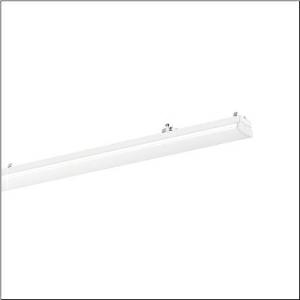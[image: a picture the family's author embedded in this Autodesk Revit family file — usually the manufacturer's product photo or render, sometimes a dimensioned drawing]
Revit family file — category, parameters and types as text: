
# Revit family: licross_r__11_recessed_opal_ho_51te1ddn46xm_35a1
name_source: partatom
category: Lighting Fixtures
units: mm (PartAtom-declared; Revit-internal decimal feet)

## family parameters
Cut with Voids When Loaded = No
Host = Face
Light Source = No
Part Type = Normal
Room Calculation Point = No
Round Connector Dimension = Use Diameter
Shared = No

## types (1)
- --- (1 x LED, 6320 lm, 33.5 W, 4000K)
    Apparent Load = 34 VA
    CIE Flux Codes = 44 73 91 87 100
    Color Rendering = 80
    Color Temperature = 4000K
    Default Elevation = 1800 mm
    Description = Licross® 11 recessed opal HO, luminaire insert, of sheet steel, coil coated, white, length: 1.500mm, width: 76mm, height: 87mm, LED rated luminous flux: 6.320lm, light colour: 840, control gear: DALI 2, with plug, 5-pole, with phase selection, mains connection: 220..240V, AC, 50/60Hz, rated input power: 34W, halogen-free wiring, primary optical cover: cover, of PMMA, light emission: direct with ceiling illumination distribution, primary light characteristic: symmetric, protection rating (complete): IP54, insulation class (complete): insulation class I (protective earthing), certification: CE, ENEC, VDE, UKCA, protection symbol: D if used in an environment with non-conductive dust loads with corresponding accessories, impact resistance: IK06, permissible ambient temperature for indoor applications: -25..+45°C, corresponds to IFS (International Featured Standards) requirements for safety and quality in the food industry, reducing of maximum allowable ambient temperature of 5°C with ceiling mounting, LABS conformity tested according to VDMA 24364:2018-05, packaging unit: 1 piece
    Height = 83 mm
    Lamp = 1 x LED
    Lamp Light Flux = 6320 lm
    Lamp Power = 33.5 W
    Lamp count = 1
    Length = 1500 mm
    Luminous efficacy = 189 lm/W
    Manufacturer = Siteco
    ModVariant = No
    Model = 51TE1DDN46XM
    Mounting Place = Ceiling
    Mounting Type = Pendant
    Number of Poles = 1
    OnlyDefault = Yes
    Power Factor = 1
    Product Name = Licross® 11 recessed opal HO
    Product group = luminaire insert
    ProductGroupID = 902
    Protection Class = Protection class I
    Protection Degree = IP 54
    RLX_Detail_Level = 1
    RLX_Emergency_Light_Flux = 0 lm
    RLX_Emergency_Type = 0
    RLX_Emergency_Type_DB = No
    RlxData = <blob elided: 26813 chars, md5=9634553b>
    Socket = socket
    Standby Power = 0 W
    System Light Flux = 6320 lm
    System Power = 34 W
    Type Comments = factory setting: luminous flux: 100 % | dim-lin: 254 | 232 mA
    Type Image = l_1313666.jpg
    URL = http://relux.com
    VarID = @adj_075906
    Voltage = 0 V
    Weight = 0.00 kg
    Width = 76 mm

## geometry (parser evidence)
native form markers: Blend x4, Sweep x14
no freeform markers — native parametric forms only
